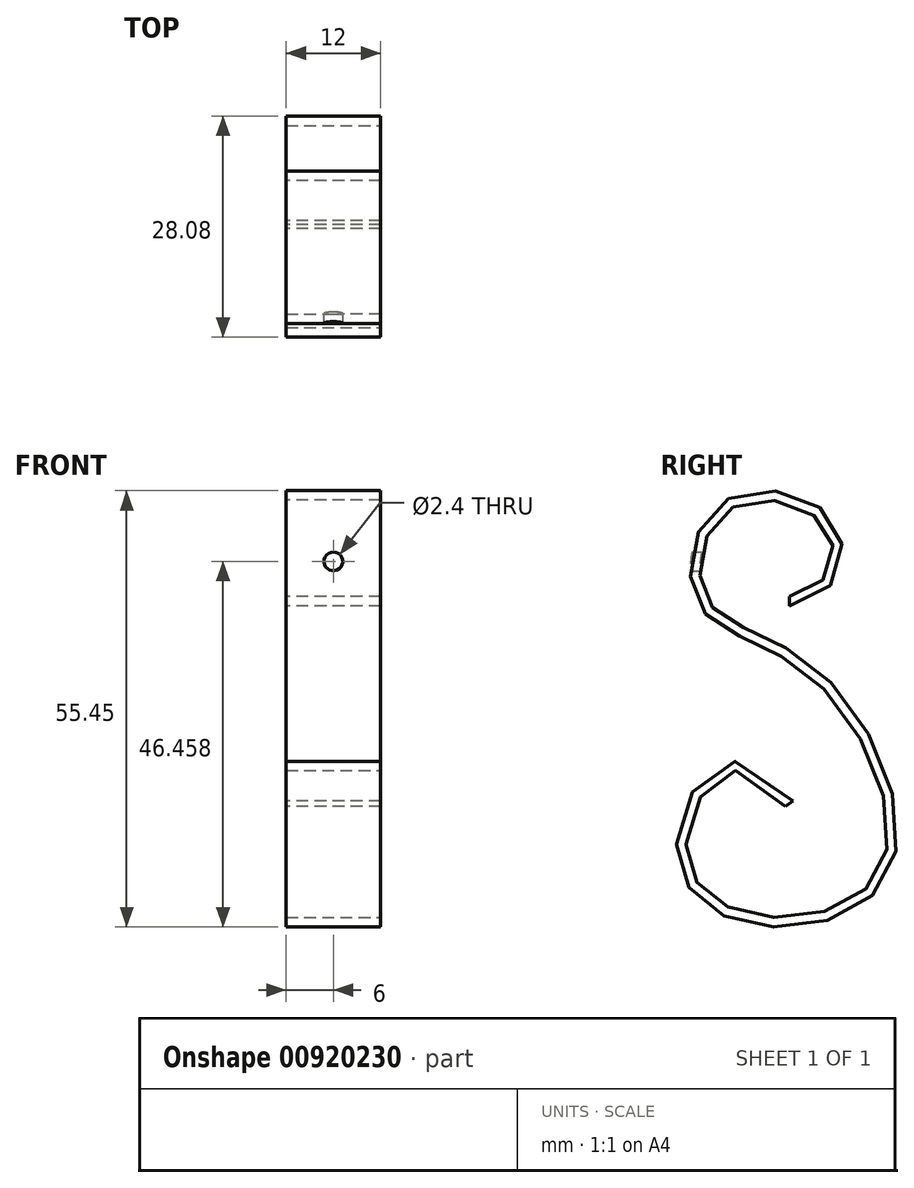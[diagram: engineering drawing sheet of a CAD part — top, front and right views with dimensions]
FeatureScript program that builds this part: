
annotation { "Feature Type Name" : "Feature", "Feature Type Description" : "" }
export const myFeature = defineFeature(function(context is Context, id is Id, definition is map)
    precondition{}
    {
        {
            var Q0;
            Q0=qCreatedBy(makeId("Right.planeOp"),FACE);
            var sketch = newSketch(context, id + "F0", { "sketchPlane" : qUnion([Q0])});
            skFitSpline(sketch, "E0", {"points": [v(0, 0) * mm, v(5.63, 8.93) * mm, v(-7.79, 12.27) * mm, v(-11.06, 0) * mm, v(2.97, -8.96) * mm, v(12.21, -34.21) * mm, v(-5.79, -40.22) * mm, v(-13.54, -29.21) * mm, v(0, -25.72) * mm], "startDerivative": vector(141.66, 0) * mm, "endDerivative": vector(171.9, -250.14) * mm});
            skSolve(sketch);
        }
        {
            var Q0;
            Q0=qCreatedBy(makeId("Front.planeOp"),FACE);
            var sketch = newSketch(context, id + "F1", { "sketchPlane" : qUnion([Q0])});
            skLineSegment(sketch, "E1.bottom", {"start": v(6, -0.6) * mm, "end": v(-6, -0.6) * mm});
            skLineSegment(sketch, "E1.top", {"start": v(6, 0.6) * mm, "end": v(-6, 0.6) * mm});
            skLineSegment(sketch, "E1.left", {"start": v(6, -0.6) * mm, "end": v(6, 0.6) * mm});
            skLineSegment(sketch, "E1.right", {"start": v(-6, -0.6) * mm, "end": v(-6, 0.6) * mm});
            skPoint(sketch, "E1.middle", {"position": v(0, 0) * mm});
            skSolve(sketch);
        }
        {
            var Q0;
            Q0=makeQuery(id+"F1.imprint","IMPRINT",FACE,{"disambiguationData":[TD([[makeQuery(id+"F1.imprint","IMPRINT",EDGE,{"derivedFrom":sQuery(id+"F1.wireOp",EDGE,"E1.bottom")}),-1.0]])]});
            var Q1;
            Q1=sQuery(id+"F0.wireOp",EDGE,"E0");
            sweep(context, id + "F2", {"profiles" : qUnion([Q0]), "path" : qUnion([Q1])});
        }
        {
            var Q0;
            Q0=qCreatedBy(makeId("Front.planeOp"),FACE);
            var sketch = newSketch(context, id + "F3", { "sketchPlane" : qUnion([Q0])});
            skCircle(sketch, "E2", {"center": v(0, 5.05) * mm, "radius": 1.2 * mm});
            skSolve(sketch);
        }
        {
            var Q0;
            Q0 = qSketchRegion(id + "F3", true);
            extrude(context, id + "F4", {"entities" : qUnion([Q0]), "operationType" : NewBodyOperationType.REMOVE, "depth" : 25.5 * mm, "offsetDistance" : 25 * mm});
        }
    });
